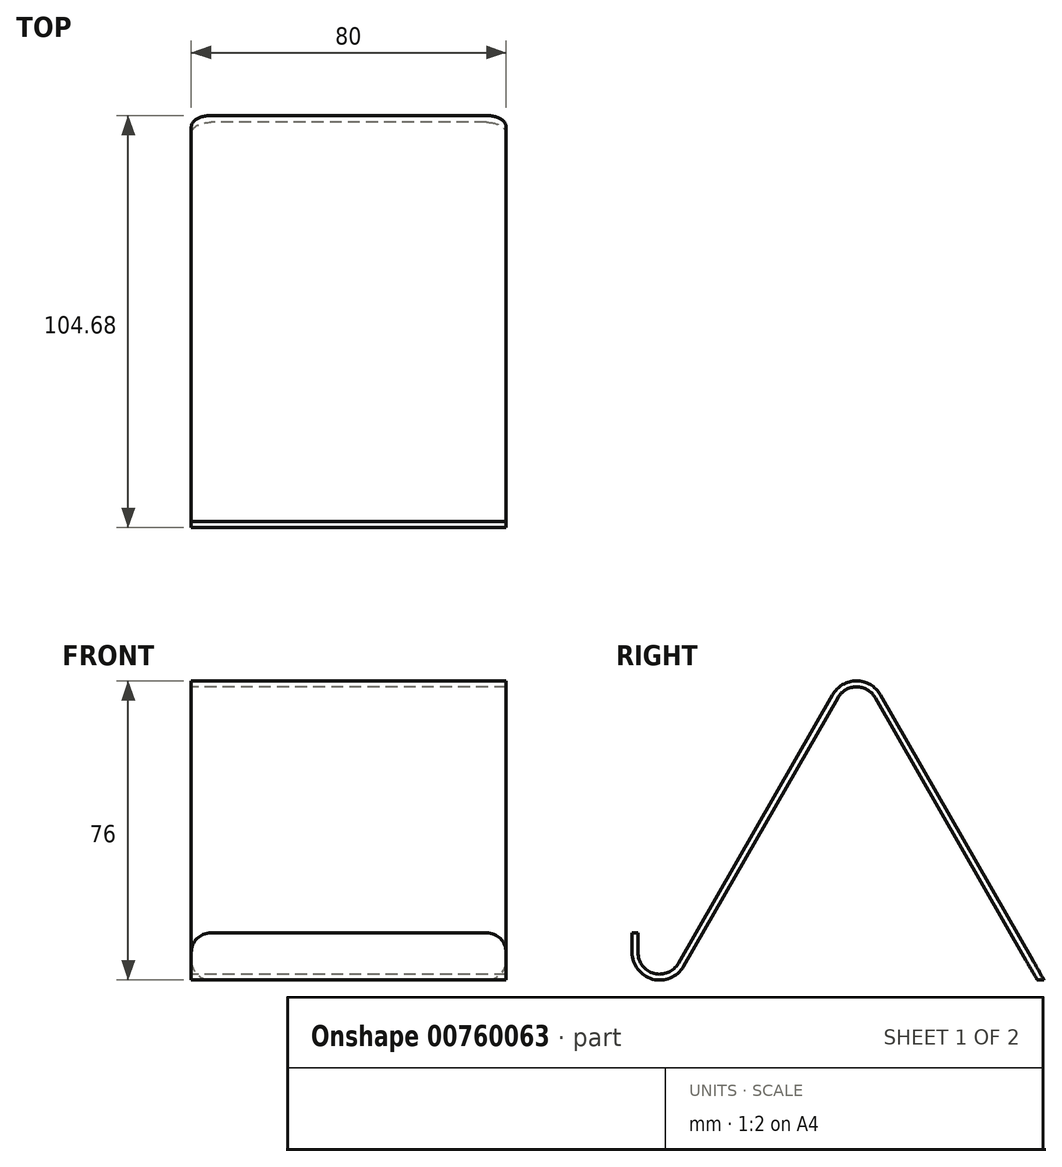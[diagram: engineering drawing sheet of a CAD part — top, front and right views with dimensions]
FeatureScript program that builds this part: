
annotation { "Feature Type Name" : "Feature", "Feature Type Description" : "" }
export const myFeature = defineFeature(function(context is Context, id is Id, definition is map)
    precondition{}
    {
        {
            var Q0;
            Q0=qCreatedBy(makeId("Right.planeOp"),FACE);
            var sketch = newSketch(context, id + "F0", { "sketchPlane" : qUnion([Q0])});
            skArc(sketch, "E0", {"start": v(-7, 0) * mm, "mid": v(-1.8, -6.76) * mm, "end": v(6.07, -3.48) * mm});
            skArc(sketch, "E1", {"start": v(54.77, 64.74) * mm, "mid": v(50, 67.5) * mm, "end": v(45.23, 64.74) * mm});
            skLineSegment(sketch, "E2", {"start": v(6.07, -3.48) * mm, "end": v(45.23, 64.74) * mm});
            skLineSegment(sketch, "E3", {"start": v(50, 62) * mm, "end": v(50, 0) * mm, "construction": true});
            skLineSegment(sketch, "E4.MirrorCS", {"start": v(95.95, -7) * mm, "end": v(54.77, 64.74) * mm});
            skLineSegment(sketch, "E5", {"start": v(0, -7) * mm, "end": v(110.77, -7) * mm, "construction": true});
            skLineSegment(sketch, "E6", {"start": v(-7, 0) * mm, "end": v(-7, 5) * mm});
            skLineSegment(sketch, "E7.0", {"start": v(-5.5, 0) * mm, "end": v(-5.5, 5) * mm});
            skLineSegment(sketch, "E7.1", {"start": v(97.68, -7) * mm, "end": v(56.07, 65.48) * mm});
            skArc(sketch, "E7.2", {"start": v(56.07, 65.48) * mm, "mid": v(50, 69) * mm, "end": v(43.93, 65.48) * mm});
            skLineSegment(sketch, "E7.3", {"start": v(4.77, -2.74) * mm, "end": v(43.93, 65.48) * mm});
            skArc(sketch, "E7.4", {"start": v(-5.5, 0) * mm, "mid": v(-1.42, -5.31) * mm, "end": v(4.77, -2.74) * mm});
            skLineSegment(sketch, "E8", {"start": v(-7, 5) * mm, "end": v(-5.5, 5) * mm});
            skLineSegment(sketch, "E9", {"start": v(95.95, -7) * mm, "end": v(97.68, -7) * mm});
            skSolve(sketch);
        }
        {
            var Q0;
            Q0=qSketchRegion(id+"F0",true);
            extrude(context, id + "F1", {"entities" : qUnion([Q0]), "endBound" : BoundingType.SYMMETRIC, "depth" : 80 * mm, "offsetDistance" : 25 * mm});
        }
        {
            var Q0;
            Q0=makeQuery(id+"F1.opExtrude","CAP_EDGE",EDGE,{"disambiguationData":[OSD([sQuery(id+"F0.wireOp",EDGE,"E8")])],"isStart":false});
            var Q1;
            Q1=makeQuery(id+"F1.opExtrude","CAP_EDGE",EDGE,{"disambiguationData":[OSD([sQuery(id+"F0.wireOp",EDGE,"E8")])],"isStart":true});
            var Q2;
            Q2=makeQuery(id+"F1.opExtrude","CAP_EDGE",EDGE,{"disambiguationData":[OSD([sQuery(id+"F0.wireOp",EDGE,"E9")])],"isStart":false});
            var Q3;
            Q3=makeQuery(id+"F1.opExtrude","CAP_EDGE",EDGE,{"disambiguationData":[OSD([sQuery(id+"F0.wireOp",EDGE,"E9")])],"isStart":true});
            fillet(context, id + "F2", {"entities" : qUnion([Q0, Q1, Q2, Q3]), "radius" : 5 * mm, "tangentPropagation" : true, "allowEdgeOverflow" : false});
        }
    });
